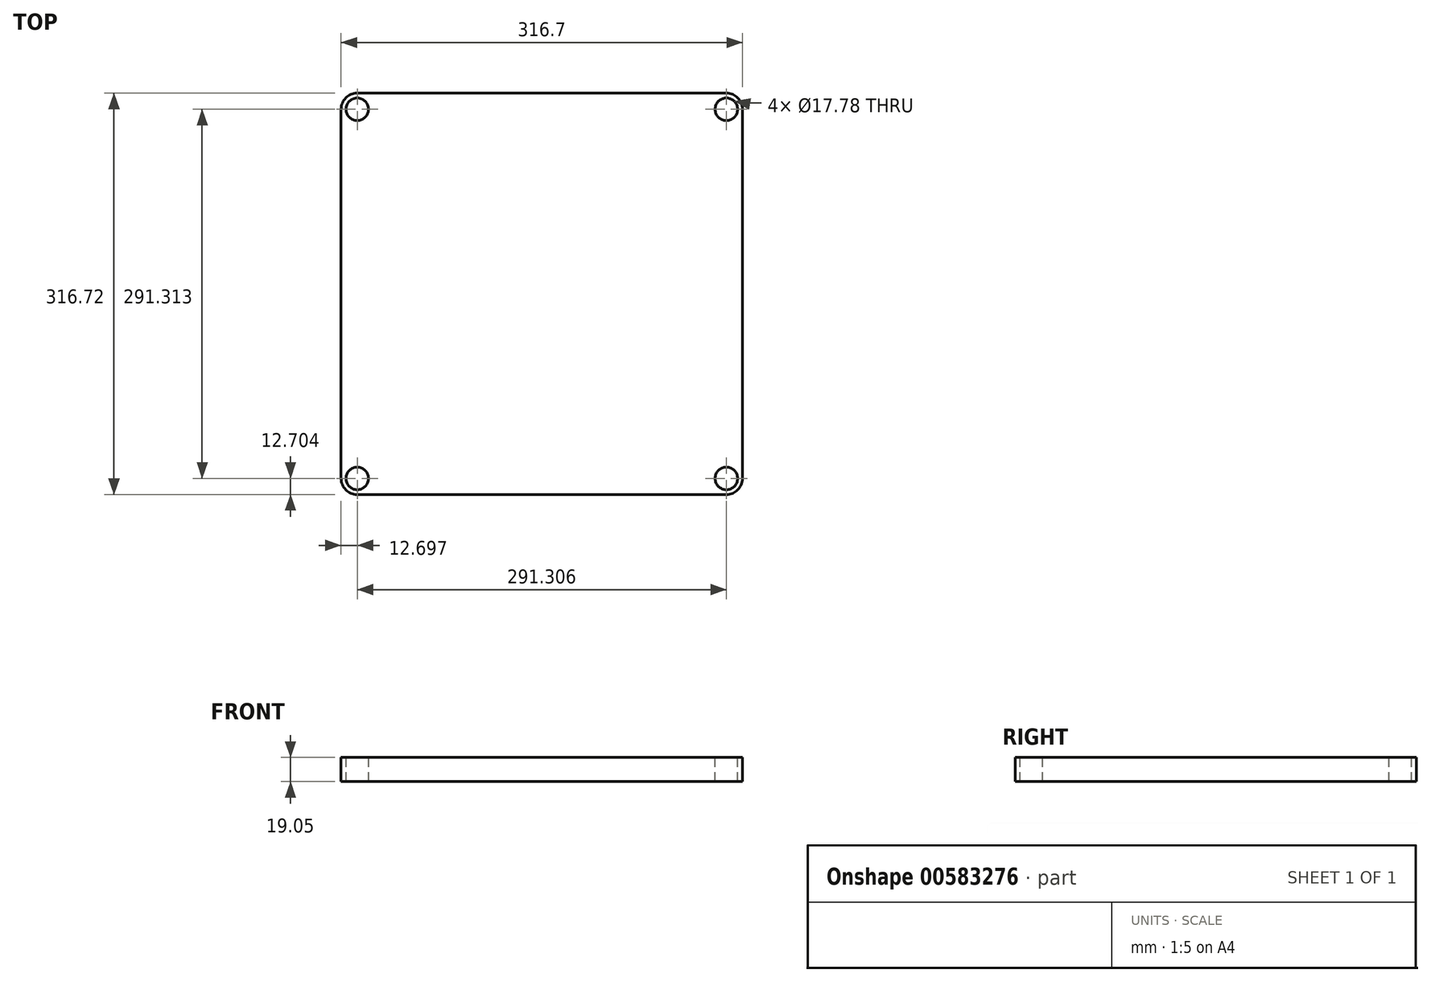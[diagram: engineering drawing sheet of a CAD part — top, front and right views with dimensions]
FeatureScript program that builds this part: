
annotation { "Feature Type Name" : "Feature", "Feature Type Description" : "" }
export const myFeature = defineFeature(function(context is Context, id is Id, definition is map)
    precondition{}
    {
        {
            var Q0;
            Q0=qCreatedBy(makeId("Top.planeOp"),FACE);
            var sketch = newSketch(context, id + "F0", { "sketchPlane" : qUnion([Q0])});
            skLineSegment(sketch, "E0.bottom", {"start": v(158.35, 158.36) * mm, "end": v(-158.35, 158.36) * mm});
            skLineSegment(sketch, "E0.top", {"start": v(158.35, -158.36) * mm, "end": v(-158.35, -158.36) * mm});
            skLineSegment(sketch, "E0.left", {"start": v(158.35, 158.36) * mm, "end": v(158.35, -158.36) * mm});
            skLineSegment(sketch, "E0.right", {"start": v(-158.35, 158.36) * mm, "end": v(-158.35, -158.36) * mm});
            skPoint(sketch, "E0.middle", {"position": v(0, 0) * mm});
            skSolve(sketch);
        }
        {
            var Q0;
            Q0=makeQuery(id+"F0.imprint","IMPRINT",FACE,{"disambiguationData":[TD([[makeQuery(id+"F0.imprint","IMPRINT",EDGE,{"derivedFrom":sQuery(id+"F0.wireOp",EDGE,"E0.bottom")}),1.0]])]});
            extrude(context, id + "F1", {"entities" : qUnion([Q0]), "depth" : 19.05 * mm, "offsetDistance" : 25.4 * mm});
        }
        {
            var Q0;
            Q0=makeQuery(id+"F1.opExtrude","SWEPT_EDGE",EDGE,{"disambiguationData":[OSD([sQuery(id+"F0.wireOp",EDGE,"E0.top"),sQuery(id+"F0.wireOp",EDGE,"E0.right")])]});
            var Q1;
            Q1=makeQuery(id+"F1.opExtrude","SWEPT_EDGE",EDGE,{"disambiguationData":[OSD([sQuery(id+"F0.wireOp",EDGE,"E0.bottom"),sQuery(id+"F0.wireOp",EDGE,"E0.right")])]});
            var Q2;
            Q2=makeQuery(id+"F1.opExtrude","SWEPT_EDGE",EDGE,{"disambiguationData":[OSD([sQuery(id+"F0.wireOp",EDGE,"E0.bottom"),sQuery(id+"F0.wireOp",EDGE,"E0.left")])]});
            var Q3;
            Q3=makeQuery(id+"F1.opExtrude","SWEPT_EDGE",EDGE,{"disambiguationData":[OSD([sQuery(id+"F0.wireOp",EDGE,"E0.top"),sQuery(id+"F0.wireOp",EDGE,"E0.left")])]});
            fillet(context, id + "F2", {"entities" : qUnion([Q0, Q1, Q2, Q3]), "radius" : 12.7 * mm, "tangentPropagation" : true, "allowEdgeOverflow" : false});
        }
        {
            var Q0;
            Q0=makeQuery(id+"F1.opExtrude","CAP_FACE",FACE,{"disambiguationData":[OSD([sQuery(id+"F0.wireOp",EDGE,"E0.bottom"),sQuery(id+"F0.wireOp",EDGE,"E0.top"),sQuery(id+"F0.wireOp",EDGE,"E0.left"),sQuery(id+"F0.wireOp",EDGE,"E0.right")])],"isStart":false});
            var sketch = newSketch(context, id + "F3", { "sketchPlane" : qUnion([Q0])});
            skCircle(sketch, "E1", {"center": v(-145.65, 145.66) * mm, "radius": 8.9 * mm});
            skCircle(sketch, "E2.MirrorC", {"center": v(145.65, 145.66) * mm, "radius": 8.9 * mm});
            skCircle(sketch, "E3.MirrorC", {"center": v(145.65, -145.66) * mm, "radius": 8.9 * mm});
            skCircle(sketch, "E4.MirrorC", {"center": v(-145.65, -145.66) * mm, "radius": 8.9 * mm});
            skSolve(sketch);
        }
        {
            var Q0;
            Q0=qSketchRegion(id+"F3",true);
            extrude(context, id + "F4", {"entities" : qUnion([Q0]), "operationType" : NewBodyOperationType.REMOVE, "oppositeDirection" : true, "depth" : 25.4 * mm, "offsetDistance" : 25.4 * mm});
        }
    });
